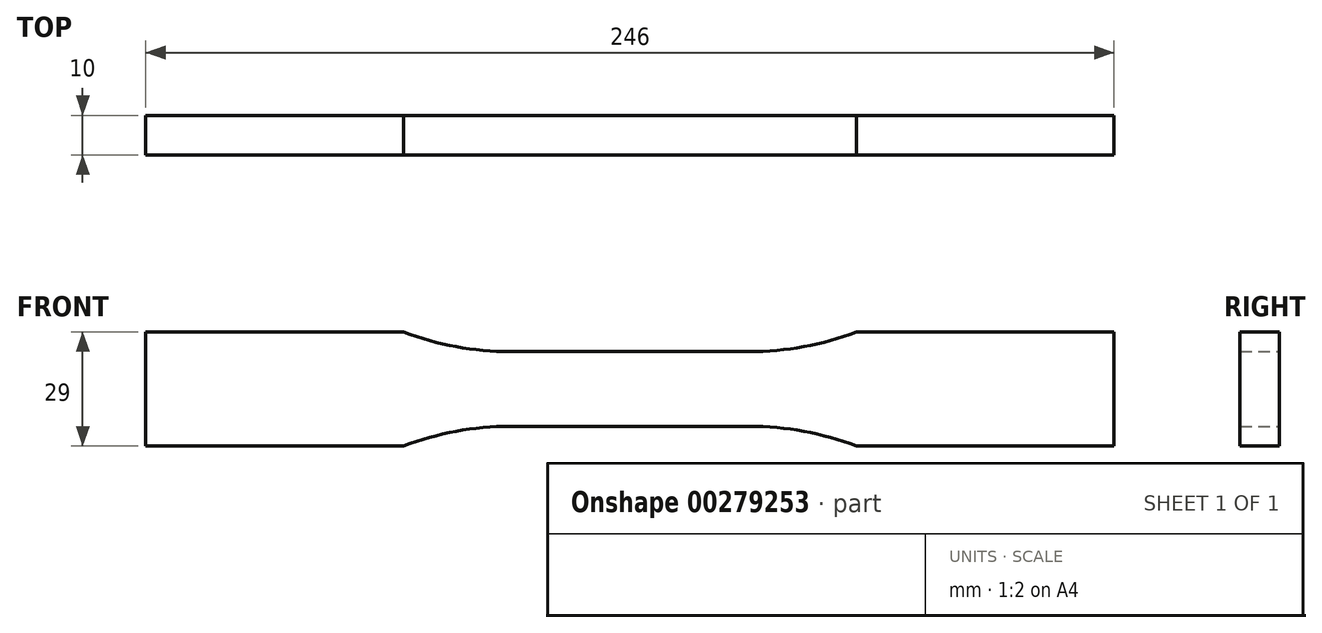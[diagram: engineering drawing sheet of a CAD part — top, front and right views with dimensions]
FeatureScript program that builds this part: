
annotation { "Feature Type Name" : "Feature", "Feature Type Description" : "" }
export const myFeature = defineFeature(function(context is Context, id is Id, definition is map)
    precondition{}
    {
        {
            var Q0;
            Q0=qCreatedBy(makeId("Front.planeOp"),FACE);
            var sketch = newSketch(context, id + "F0", { "sketchPlane" : qUnion([Q0])});
            skLineSegment(sketch, "E0", {"start": v(0, 9.5) * mm, "end": v(30.39, 9.5) * mm});
            skArc(sketch, "E1", {"start": v(30.39, 9.5) * mm, "mid": v(44.17, 10.76) * mm, "end": v(57.5, 14.5) * mm});
            skLineSegment(sketch, "E2", {"start": v(57.5, 14.5) * mm, "end": v(123, 14.5) * mm});
            skLineSegment(sketch, "E3.MirrorCS", {"start": v(0, -9.5) * mm, "end": v(30.39, -9.5) * mm});
            skLineSegment(sketch, "E4.MirrorCS", {"start": v(57.5, -14.5) * mm, "end": v(123, -14.5) * mm});
            skArc(sketch, "E5.MirrorCS", {"start": v(30.39, -9.5) * mm, "mid": v(44.17, -10.76) * mm, "end": v(57.5, -14.5) * mm});
            skArc(sketch, "E6.MirrorCS", {"start": v(-30.39, -9.5) * mm, "mid": v(-44.17, -10.76) * mm, "end": v(-57.5, -14.5) * mm});
            skLineSegment(sketch, "E7.MirrorCS", {"start": v(0, 9.5) * mm, "end": v(-30.39, 9.5) * mm});
            skArc(sketch, "E8.MirrorCS", {"start": v(-30.39, 9.5) * mm, "mid": v(-44.17, 10.76) * mm, "end": v(-57.5, 14.5) * mm});
            skLineSegment(sketch, "E9.MirrorCS", {"start": v(0, -9.5) * mm, "end": v(-30.39, -9.5) * mm});
            skLineSegment(sketch, "E10.MirrorCS", {"start": v(-57.5, 14.5) * mm, "end": v(-123, 14.5) * mm});
            skLineSegment(sketch, "E11.MirrorCS", {"start": v(-57.5, -14.5) * mm, "end": v(-123, -14.5) * mm});
            skLineSegment(sketch, "E12", {"start": v(-123, 14.5) * mm, "end": v(-123, -14.5) * mm});
            skLineSegment(sketch, "E13", {"start": v(123, 14.5) * mm, "end": v(123, -14.5) * mm});
            skSolve(sketch);
        }
        {
            var Q0;
            Q0 = qSketchRegion(id + "F0", true);
            extrude(context, id + "F1", {"entities" : qUnion([Q0]), "endBound" : BoundingType.SYMMETRIC, "depth" : 10 * mm});
        }
    });
